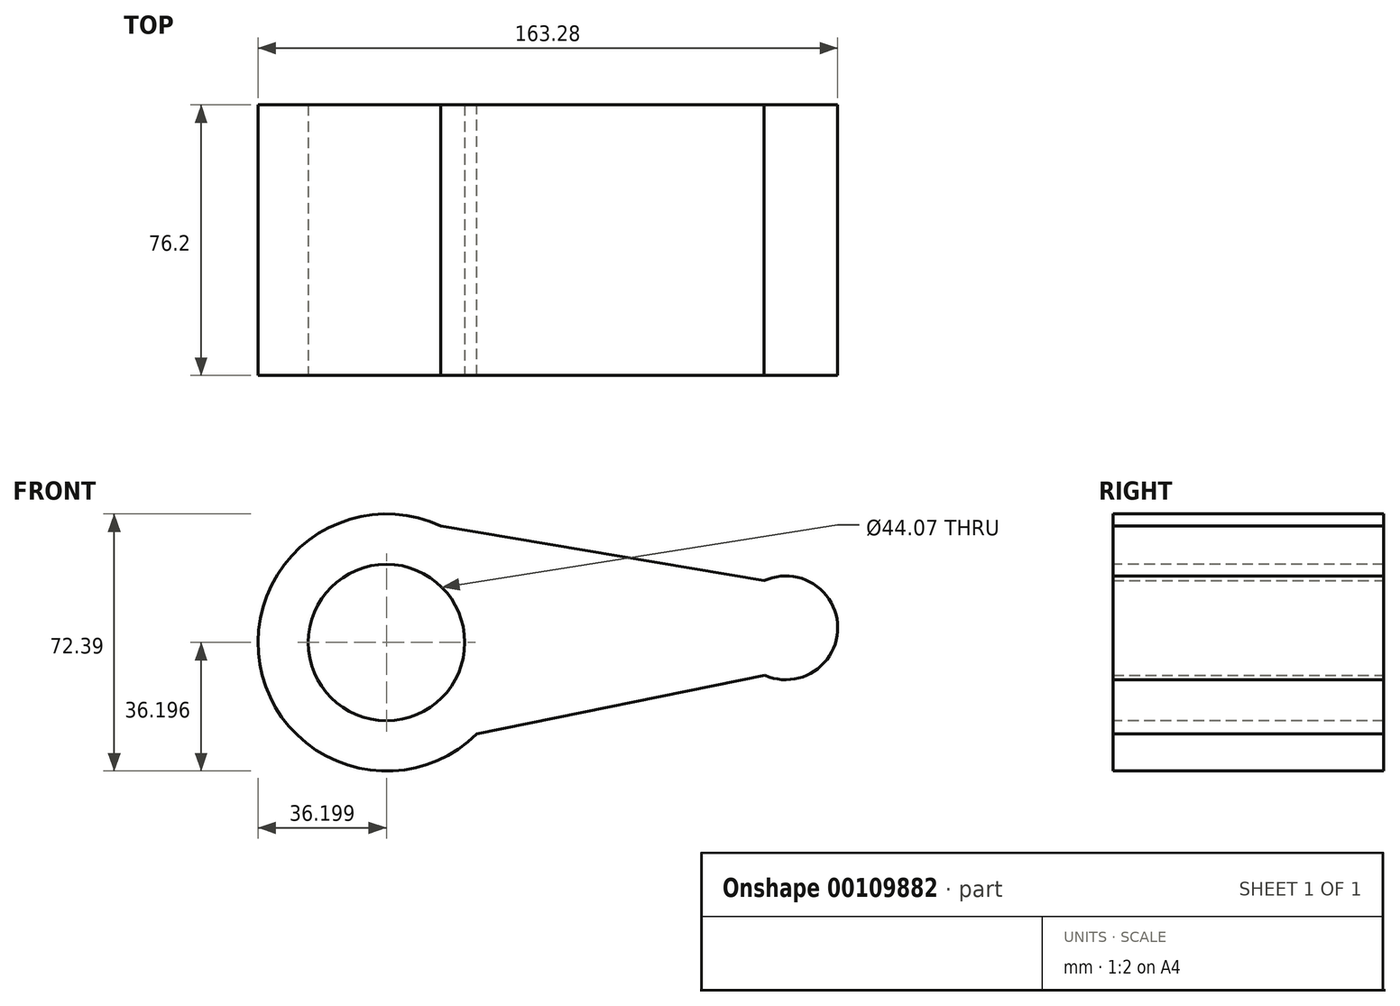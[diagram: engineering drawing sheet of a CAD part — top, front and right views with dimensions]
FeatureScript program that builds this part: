
annotation { "Feature Type Name" : "Feature", "Feature Type Description" : "" }
export const myFeature = defineFeature(function(context is Context, id is Id, definition is map)
    precondition{}
    {
        {
            var Q0;
            Q0=qCreatedBy(makeId("Front.planeOp"),FACE);
            var sketch = newSketch(context, id + "F0", { "sketchPlane" : qUnion([Q0])});
            skCircle(sketch, "E0", {"center": v(-45.71, -12.4) * mm, "radius": 36.2 * mm});
            skLineSegment(sketch, "E1", {"start": v(-30.37, 20.39) * mm, "end": v(60.62, 5.01) * mm});
            skLineSegment(sketch, "E2", {"start": v(-20.3, -38.17) * mm, "end": v(60.9, -21.64) * mm});
            skCircle(sketch, "E3", {"center": v(66.76, -8.25) * mm, "radius": 14.61 * mm});
            skSolve(sketch);
        }
        {
            var Q0;
            Q0 = qSketchRegion(id + "F0", true);
            extrude(context, id + "F1", {"entities" : qUnion([Q0]), "depth" : 76.2 * mm});
        }
        {
            var Q0;
            Q0=makeQuery(id+"F1.opExtrude","CAP_FACE",FACE,{"disambiguationData":[OSD([sQuery(id+"F0.wireOp",EDGE,"E0"),sQuery(id+"F0.wireOp",EDGE,"E1"),sQuery(id+"F0.wireOp",EDGE,"E2"),sQuery(id+"F0.wireOp",EDGE,"E3")])],"isStart":false});
            var sketch = newSketch(context, id + "F2", { "sketchPlane" : qUnion([Q0])});
            skCircle(sketch, "E4", {"center": v(-45.71, -12.4) * mm, "radius": 22.03 * mm});
            skSolve(sketch);
        }
        {
            var Q0;
            Q0 = qSketchRegion(id + "F2", true);
            extrude(context, id + "F3", {"entities" : qUnion([Q0]), "operationType" : NewBodyOperationType.REMOVE, "oppositeDirection" : true, "depth" : 254 * mm});
        }
    });
